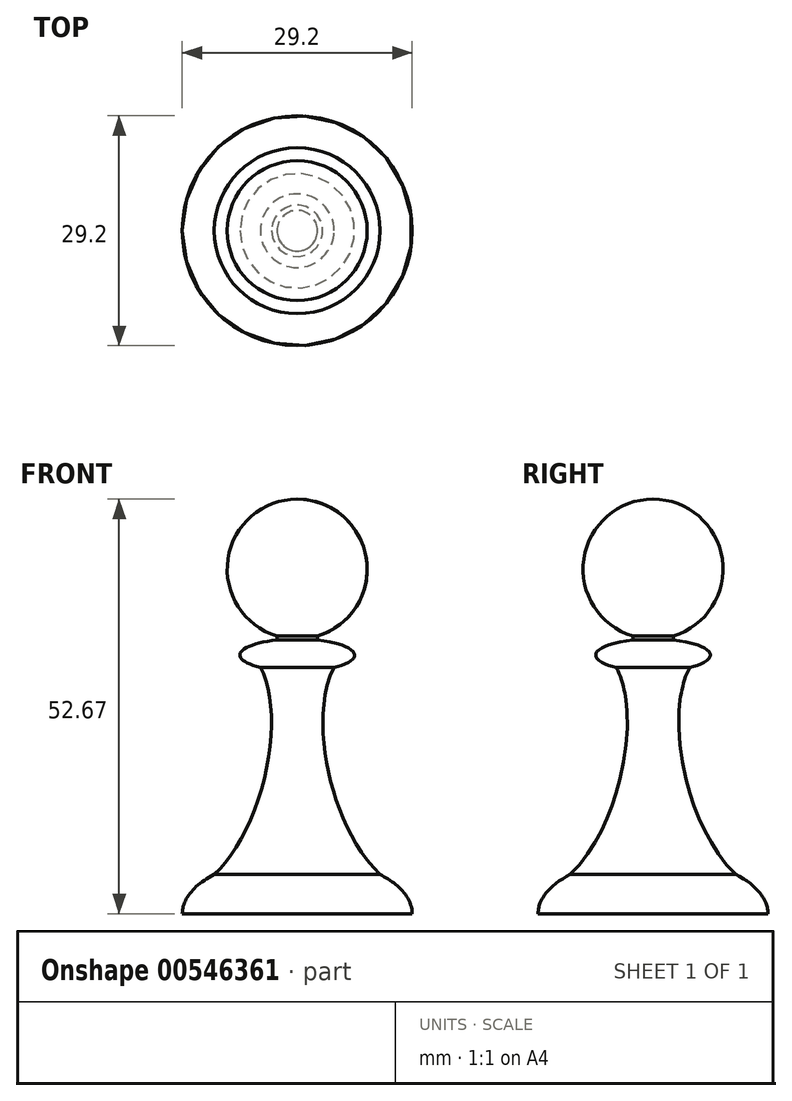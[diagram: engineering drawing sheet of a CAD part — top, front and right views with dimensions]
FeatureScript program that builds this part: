
annotation { "Feature Type Name" : "Feature", "Feature Type Description" : "" }
export const myFeature = defineFeature(function(context is Context, id is Id, definition is map)
    precondition{}
    {
        {
            var Q0;
            Q0=qCreatedBy(makeId("Front.planeOp"),FACE);
            var sketch = newSketch(context, id + "F0", { "sketchPlane" : qUnion([Q0])});
            skLineSegment(sketch, "E0", {"start": v(0, 0) * mm, "end": v(0, 52.67) * mm});
            skArc(sketch, "E1", {"start": v(0, 52.67) * mm, "mid": v(-8.8, 45.08) * mm, "end": v(-2.58, 35.27) * mm});
            skEllipticalArc(sketch, "E2", {});
            skEllipticalArc(sketch, "E3", {});
            skEllipticalArc(sketch, "E4", {});
            skLineSegment(sketch, "E5", {"start": v(0, 0) * mm, "end": v(-14.6, 0) * mm});
            skLineSegment(sketch, "E6", {"start": v(-2.58, 35.27) * mm, "end": v(-2.58, 34.76) * mm});
            skPoint(sketch, "E7.orphan", {"position": v(0, 34.89) * mm});
            const initialGuessF0  = {"E2": [0, 0.032857471128346125, -1, 0, 0.007282325151310642, 0.002032, 5.0741121571530545, 0.8728902685310416], "E3": [-0.01148394588381052, 0.018441645428538322, -0.25629508420816555, -0.9665985877347066, 0.015813724575141665, 0.0073983001606599584, 0.6319081519198813, 2.6820746422833057], "E4": [0, 0, -1, 0, 0.014599903486669064, 0.007200652743311954, 5.517996199717742, 0]};
            skSetInitialGuess(sketch, initialGuessF0);
            skSolve(sketch);
        }
        {
            var Q0;
            Q0=makeQuery(id+"F0.imprint","IMPRINT",FACE,{"disambiguationData":[TD([[makeQuery(id+"F0.imprint","IMPRINT",EDGE,{"derivedFrom":sQuery(id+"F0.wireOp",EDGE,"E0")}),1.0]])]});
            var Q1;
            Q1=sQuery(id+"F0.wireOp",EDGE,"E0");
            revolve(context, id + "F1", {"entities" : qUnion([Q0]), "axis" : qUnion([Q1]), "revolveType" : RevolveType.FULL});
        }
    });
